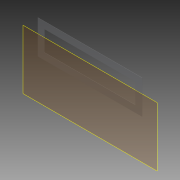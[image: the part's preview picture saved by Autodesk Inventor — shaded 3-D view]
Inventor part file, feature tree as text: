
AUTODESK INVENTOR PART (.ipt)
format: ipt  version: 2013 (Build 170138000, 138)  size: 91,648 bytes
history: native  units: in
note: dims shown in document units (in); Inventor stores cm internally (conversion verified against a paired STEP export)
features: reference x6, plane x1, extrude x1, sketch x1
ambient origin geometry x8: Origin, YZ Plane, XZ Plane, XY Plane, X Axis, Y Axis, Z Axis, Center Point
bodies: Solid1 (feature_tree)
feature tree (9):
  plane  "Work Plane1"
  extrude  "Extrusion1"  Depth=0.1in TaperAngle=0.0deg
  sketch  "Sketch1"  dims[d0=4.0in d1=0.1in d2=0.0in]
  reference  "Reference1"
  reference  "Reference2"
  reference  "Reference3"
  reference  "Reference4"
  reference  "Reference5"
  reference  "Reference6"
